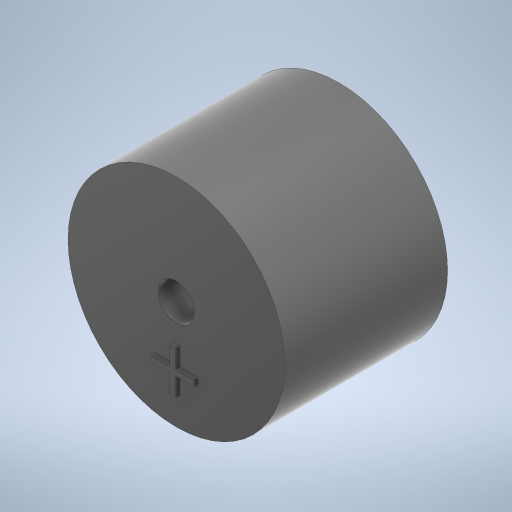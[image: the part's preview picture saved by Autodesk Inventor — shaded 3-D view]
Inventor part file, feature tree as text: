
AUTODESK INVENTOR PART (.ipt)
format: ipt  version: 2024.3 (Build 283343000, 343)  size: 248,832 bytes
history: native  units: mm
features: extrude x3, sketch x2
ambient origin geometry x8: Origin, YZ Plane, XZ Plane, XY Plane, X Axis, Y Axis, Z Axis, Center Point
bodies: Solid1 (feature_tree)
feature tree (5):
  extrude  "Extrusion1"  Depth=9.0mm TaperAngle=0.0deg
  sketch  "Sketch2"  dims[d3=2.0mm d4=5.0mm d5=0.0mm d6=0.2mm d7=0.0mm]
  extrude  "Extrusion2"  Depth=5.0mm TaperAngle=0.0deg
  extrude  "Extrusion3"  Depth=0.2mm TaperAngle=0.0deg
  sketch  "Sketch1"  dims[d0=12.0mm d1=9.0mm d2=0.0mm]
